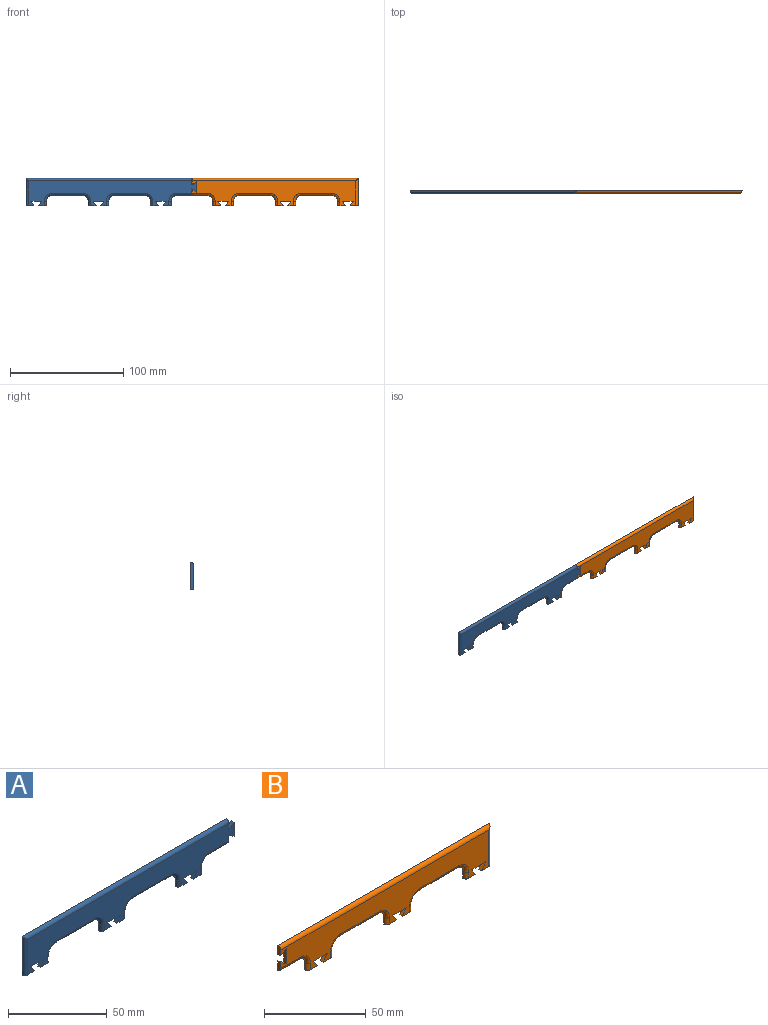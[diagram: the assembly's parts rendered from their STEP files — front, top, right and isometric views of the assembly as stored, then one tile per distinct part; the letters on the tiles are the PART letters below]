
ASSEMBLY  parts=2 mates=1
PART A: 37 faces, bbox 150.2x3.4x24 mm
  f0: plane 5.65x2mm, normal (1,0,0), area 10.4mm2, adj f17,f18,f20,f27
  f1: plane 7x2mm, normal (0,0,-1), area 13.1mm2, adj f2,f17,f18,f22
  f2: plane 4x2.8mm, normal (0.82,0,0.57), area 9.8mm2, adj f1,f3,f17,f18
  f3: plane 9.6x2mm, normal (0,0,-1), area 19.2mm2, adj f2,f4,f17,f18
  f4: plane 4x2.8mm, normal (-0.82,0,0.57), area 9.8mm2, adj f3,f5,f17,f18
  f5: plane 7x2mm, normal (0,0,-1), area 13.1mm2, adj f4,f17,f18,f34
  f6: plane 7x2mm, normal (0,0,-1), area 13.1mm2, adj f7,f17,f18,f30
  f7: plane 4x2.8mm, normal (0.82,0,0.57), area 9.8mm2, adj f6,f8,f17,f18
  f8: plane 9.6x2mm, normal (0,0,-1), area 19.2mm2, adj f7,f9,f17,f18
  f9: plane 4x2.8mm, normal (-0.82,0,0.57), area 9.8mm2, adj f8,f10,f17,f18
  f10: plane 7x2mm, normal (0,0,-1), area 13.1mm2, adj f9,f17,f18,f29
  f11: plane 5.65x2mm, normal (1,0,0), area 10.4mm2, adj f17,f18,f19,f35
  f12: plane 7x2mm, normal (0,0,-1), area 13.1mm2, adj f13,f17,f18,f36
  f13: plane 4x2.8mm, normal (0.82,0,0.57), area 9.8mm2, adj f12,f14,f17,f18
  f14: plane 9.6x2mm, normal (0,0,-1), area 19.2mm2, adj f13,f15,f17,f18
  f15: plane 4x2.8mm, normal (-0.82,0,0.57), area 9.8mm2, adj f14,f16,f17,f18
  f16: plane 7x2mm, normal (0,0,-1), area 13.1mm2, adj f15,f17,f18,f26
  f17: plane 148.2x22mm, normal (0,-1,0), area 2045.7mm2, adj f0,f1,f2,f3,f4,f5,f6,f7
  f18: plane 150.2x24mm, normal (0,1,0), area 2652mm2, adj f0,f1,f2,f3,f4,f5,f6,f7
  f19: plane 3.7x2.59mm, normal (-0.57,0,0.82), area 9mm2, adj f11,f17,f18,f21
  f20: plane 3.7x2.59mm, normal (-0.57,0,-0.82), area 9mm2, adj f0,f17,f18,f21
  f21: plane 8.88x2mm, normal (1,0,0), area 17.8mm2, adj f17,f18,f19,f20
  f22: cylinder r=2mm len=4mm, axis (0,0,1), area 12.6mm2, adj f1,f17,f18,f23
  f23: torus R=7mm, axis (0,-1,0), area 28.3mm2, adj f17,f18,f22,f24
  f24: cylinder r=2mm len=27mm, axis (-1,0,0), area 84.8mm2, adj f17,f18,f23,f25
  f25: torus R=7mm, axis (0,-1,0), area 28.3mm2, adj f17,f18,f24,f26
  f26: cylinder r=2mm len=4mm, axis (0,0,-1), area 12.6mm2, adj f16,f17,f18,f25
  f27: cylinder r=2mm len=13.5mm, axis (-1,0,0), area 42.4mm2, adj f0,f17,f18,f28
  f28: torus R=7mm, axis (0,-1,0), area 28.3mm2, adj f17,f18,f27,f29
  f29: cylinder r=2mm len=4mm, axis (0,0,-1), area 12.6mm2, adj f10,f17,f18,f28
  f30: cylinder r=2mm len=4mm, axis (0,0,1), area 12.6mm2, adj f6,f17,f18,f31
  f31: torus R=7mm, axis (0,-1,0), area 28.3mm2, adj f17,f18,f30,f32
  f32: cylinder r=2mm len=27mm, axis (-1,0,0), area 84.8mm2, adj f17,f18,f31,f33
  f33: torus R=7mm, axis (0,-1,0), area 28.3mm2, adj f17,f18,f32,f34
  f34: cylinder r=2mm len=4mm, axis (0,0,-1), area 12.6mm2, adj f5,f17,f18,f33
  f35: cylinder r=2mm len=146.5mm, axis (1,0,0), area 458mm2, adj f11,f17,f18,f36
  f36: cylinder r=2mm len=24mm, axis (0,0,1), area 73.1mm2, adj f12,f17,f18,f35
PART B: 37 faces, bbox 146.5x3.4x24 mm
  f0: plane 5.5x2mm, normal (-1,0,0), area 10.1mm2, adj f1,f18,f19,f36
  f1: plane 146.5x24mm, normal (0,1,0), area 2601.5mm2, adj f0,f2,f3,f4,f5,f6,f7,f8
  f2: plane 7x2mm, normal (0,0,-1), area 13.1mm2, adj f1,f3,f18,f22
  f3: plane 4x2.8mm, normal (0.82,0,0.57), area 9.8mm2, adj f1,f2,f4,f18
  f4: plane 9.6x2mm, normal (0,0,-1), area 19.2mm2, adj f1,f3,f5,f18
  f5: plane 4x2.8mm, normal (-0.82,0,0.57), area 9.8mm2, adj f1,f4,f6,f18
  f6: plane 7x2mm, normal (0,0,-1), area 13.1mm2, adj f1,f5,f18,f31
  f7: plane 7x2mm, normal (0,0,-1), area 13.1mm2, adj f1,f8,f18,f27
  f8: plane 4x2.8mm, normal (0.82,0,0.57), area 9.8mm2, adj f1,f7,f9,f18
  f9: plane 9.6x2mm, normal (0,0,-1), area 19.2mm2, adj f1,f8,f10,f18
  f10: plane 4x2.8mm, normal (-0.82,0,0.57), area 9.8mm2, adj f1,f9,f11,f18
  f11: plane 7x2mm, normal (0,0,-1), area 13.1mm2, adj f1,f10,f18,f35
  f12: plane 5.5x2mm, normal (-1,0,0), area 10.1mm2, adj f1,f18,f21,f34
  f13: plane 7x2mm, normal (0,0,-1), area 13.1mm2, adj f1,f14,f18,f32
  f14: plane 4x2.8mm, normal (0.82,0,0.57), area 9.8mm2, adj f1,f13,f15,f18
  f15: plane 9.6x2mm, normal (0,0,-1), area 19.2mm2, adj f1,f14,f16,f18
  f16: plane 4x2.8mm, normal (-0.82,0,0.57), area 9.8mm2, adj f1,f15,f17,f18
  f17: plane 7x2mm, normal (0,0,-1), area 13.1mm2, adj f1,f16,f18,f26
  f18: plane 144.5x22mm, normal (0,-1,0), area 1995.3mm2, adj f0,f2,f3,f4,f5,f6,f7,f8
  f19: plane 4x2.8mm, normal (0.57,0,-0.82), area 9.8mm2, adj f0,f1,f18,f20
  f20: plane 9.6x2mm, normal (-1,0,0), area 19.2mm2, adj f1,f18,f19,f21
  f21: plane 4x2.8mm, normal (0.57,0,0.82), area 9.8mm2, adj f1,f12,f18,f20
  f22: cylinder r=2mm len=4mm, axis (0,0,1), area 12.6mm2, adj f1,f2,f18,f23
  f23: torus R=7mm, axis (0,-1,0), area 28.3mm2, adj f1,f18,f22,f24
  f24: cylinder r=2mm len=27mm, axis (-1,0,0), area 84.8mm2, adj f1,f18,f23,f25
  f25: torus R=7mm, axis (0,-1,0), area 28.3mm2, adj f1,f18,f24,f26
  f26: cylinder r=2mm len=4mm, axis (0,0,-1), area 12.6mm2, adj f1,f17,f18,f25
  f27: cylinder r=2mm len=4mm, axis (0,0,1), area 12.6mm2, adj f1,f7,f18,f28
  f28: torus R=7mm, axis (0,-1,0), area 28.3mm2, adj f1,f18,f27,f29
  f29: cylinder r=2mm len=27mm, axis (-1,0,0), area 84.8mm2, adj f1,f18,f28,f30
  f30: torus R=7mm, axis (0,-1,0), area 28.3mm2, adj f1,f18,f29,f31
  f31: cylinder r=2mm len=4mm, axis (0,0,-1), area 12.6mm2, adj f1,f6,f18,f30
  f32: cylinder r=2mm len=4mm, axis (0,0,1), area 12.6mm2, adj f1,f13,f18,f33
  f33: torus R=7mm, axis (0,-1,0), area 28.3mm2, adj f1,f18,f32,f34
  f34: cylinder r=2mm len=13.5mm, axis (-1,0,0), area 42.4mm2, adj f1,f12,f18,f33
  f35: cylinder r=2mm len=24mm, axis (0,0,-1), area 73.1mm2, adj f1,f11,f18,f36
  f36: cylinder r=2mm len=146.5mm, axis (1,0,0), area 458mm2, adj f0,f1,f18,f35
PLACE A at identity
PLACE B t=(-34.94,0,0)mm
MATE fastened B.f12 <-> A.f0  axis (-1,0,0) through (58.32,0,24.69)mm
